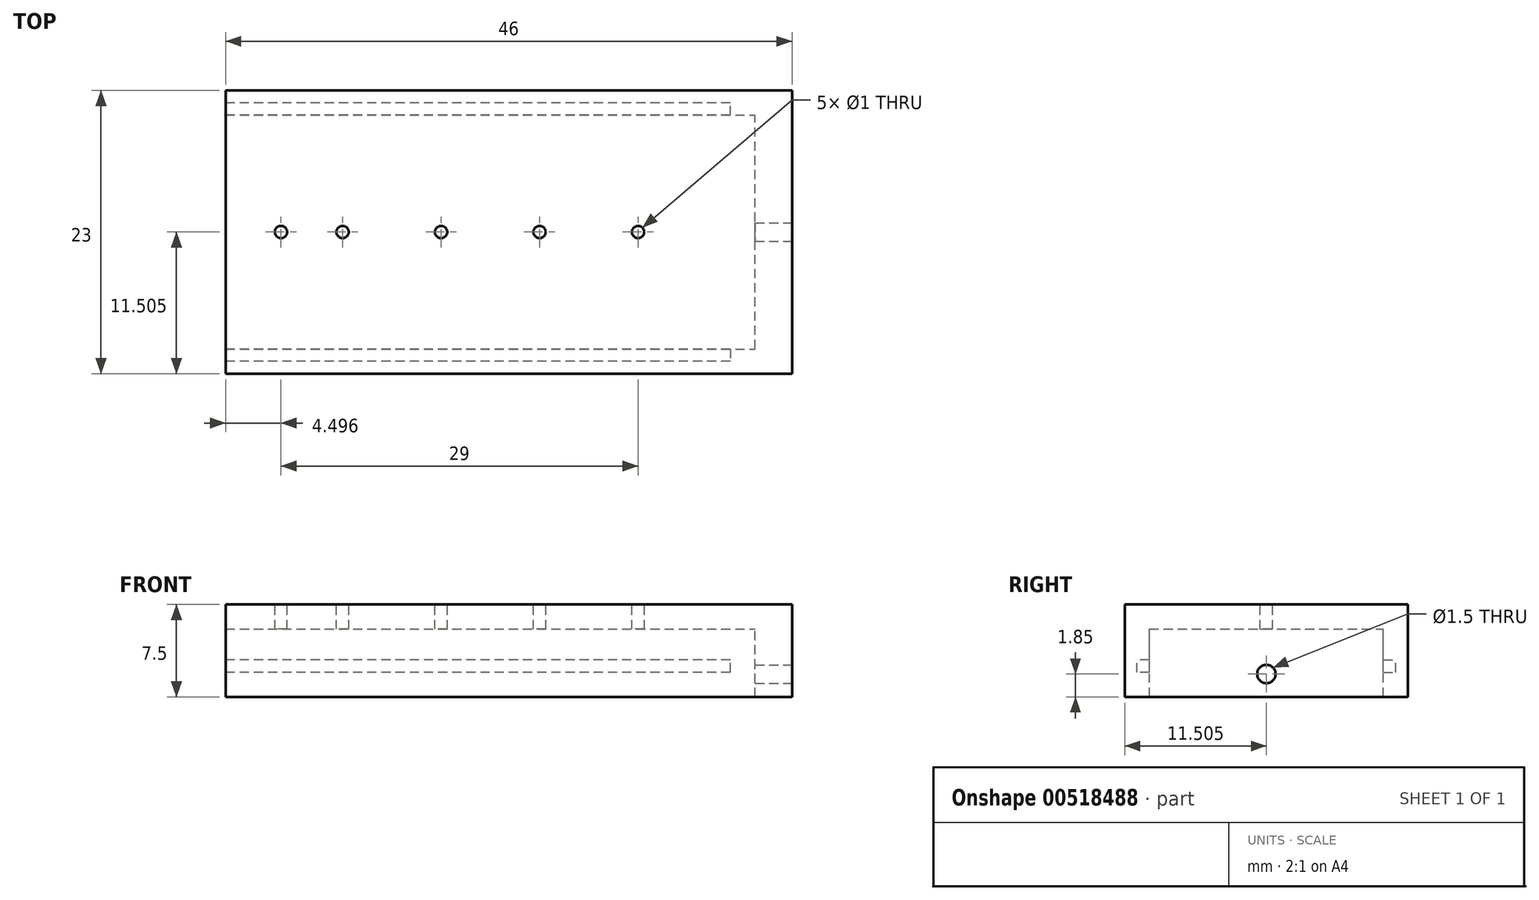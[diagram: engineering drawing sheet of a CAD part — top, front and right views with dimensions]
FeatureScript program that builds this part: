
annotation { "Feature Type Name" : "Feature", "Feature Type Description" : "" }
export const myFeature = defineFeature(function(context is Context, id is Id, definition is map)
    precondition{}
    {
        {
            var Q0;
            Q0=qCreatedBy(makeId("Top.planeOp"),FACE);
            var sketch = newSketch(context, id + "F0", { "sketchPlane" : qUnion([Q0])});
            skLineSegment(sketch, "E0.bottom", {"start": v(-4.4, -2.74) * mm, "end": v(41.6, -2.74) * mm});
            skLineSegment(sketch, "E0.top", {"start": v(-4.4, 20.26) * mm, "end": v(41.6, 20.26) * mm});
            skLineSegment(sketch, "E0.left", {"start": v(-4.4, -2.74) * mm, "end": v(-4.4, 20.26) * mm});
            skLineSegment(sketch, "E0.right", {"start": v(41.6, -2.74) * mm, "end": v(41.6, 20.26) * mm});
            skLineSegment(sketch, "E1.bottom", {"start": v(-4.4, -0.74) * mm, "end": v(38.6, -0.74) * mm});
            skLineSegment(sketch, "E1.top", {"start": v(-4.4, 18.26) * mm, "end": v(38.6, 18.26) * mm});
            skLineSegment(sketch, "E1.left", {"start": v(-4.4, -0.74) * mm, "end": v(-4.4, 18.26) * mm});
            skLineSegment(sketch, "E1.right", {"start": v(38.6, -0.74) * mm, "end": v(38.6, 18.26) * mm});
            skLineSegment(sketch, "E2", {"start": v(-5.45, 8.76) * mm, "end": v(42.38, 8.76) * mm, "construction": true});
            skPoint(sketch, "E2.startSnap0", {"position": v(-4.4, 8.76) * mm});
            skPoint(sketch, "E2.endSnap0", {"position": v(-4.4, 8.76) * mm});
            skPoint(sketch, "E3", {"position": v(38.6, 8.76) * mm});
            skPoint(sketch, "E4", {"position": v(41.6, 8.76) * mm});
            skSolve(sketch);
        }
        {
            var Q0;
            Q0=makeQuery(id+"F0.imprint","IMPRINT",FACE,{"disambiguationData":[TD([[makeQuery(id+"F0.imprint","IMPRINT",EDGE,{"derivedFrom":sQuery(id+"F0.wireOp",EDGE,"E1.bottom")}),1.0]])]});
            var Q1;
            {var subQ4=sQuery(id+"F0.wireOp",EDGE,"E0.bottom");Q1=makeQuery(id+"F0.imprint","IMPRINT",FACE,{"disambiguationData":[TD([[makeQuery(id+"F0.imprint","IMPRINT",EDGE,{"derivedFrom":subQ4}),1.0]])]});}
            extrude(context, id + "F1", {"entities" : qUnion([Q0, Q1]), "depth" : 2 * mm, "offsetDistance" : 25 * mm});
        }
        {
            var Q0;
            {var subQ4=sQuery(id+"F0.wireOp",EDGE,"E0.bottom");Q0=makeQuery(id+"F0.imprint","IMPRINT",FACE,{"disambiguationData":[TD([[makeQuery(id+"F0.imprint","IMPRINT",EDGE,{"derivedFrom":subQ4}),1.0]])]});}
            extrude(context, id + "F2", {"entities" : qUnion([Q0]), "operationType" : NewBodyOperationType.ADD, "oppositeDirection" : true, "depth" : 5.5 * mm, "offsetDistance" : 25 * mm});
        }
        {
            var Q0;
            {var subQ0=sQuery(id+"F0.wireOp",EDGE,"E0.left");var subQ1=sQuery(id+"F0.wireOp",EDGE,"E1.left");Q0=makeQuery(id+"F2.boolean.opBoolean","MERGE",FACE,{"derivedFrom":[makeQuery(id+"F1.opExtrude","SWEPT_FACE",FACE,{"disambiguationData":[OSD([subQ0,subQ1])]}),makeQuery(id+"F2.opExtrude","SWEPT_FACE",FACE,{"disambiguationData":[OSD([subQ0]),TDD([makeQuery(id+"F0.imprint","IMPRINT",EDGE,{"disambiguationData":[TD([[makeQuery(id+"F0.imprint","INTERSECT",VERTEX,{"derivedFrom":[sQuery(id+"F0.wireOp",EDGE,"E0.bottom"),subQ0]}),-1.0]])],"derivedFrom":subQ0})])]}),makeQuery(id+"F2.opExtrude","SWEPT_FACE",FACE,{"disambiguationData":[OSD([subQ0]),TDD([makeQuery(id+"F0.imprint","IMPRINT",EDGE,{"disambiguationData":[TD([[makeQuery(id+"F0.imprint","INTERSECT",VERTEX,{"derivedFrom":[sQuery(id+"F0.wireOp",EDGE,"E0.top"),subQ0]}),1.0]])],"derivedFrom":subQ0})])]})]});}
            var sketch = newSketch(context, id + "F3", { "sketchPlane" : qUnion([Q0])});
            skLineSegment(sketch, "E5", {"start": v(-8.76, 1.64) * mm, "end": v(-8.76, -7.83) * mm, "construction": true});
            skPoint(sketch, "E5.startSnap0", {"position": v(-8.76, 0) * mm});
            skPoint(sketch, "E6.oppositeSnap0", {"position": v(-18.26, -2.5) * mm});
            skLineSegment(sketch, "E6.bottom", {"start": v(-18.26, -3.5) * mm, "end": v(-19.26, -3.5) * mm});
            skLineSegment(sketch, "E6.top", {"start": v(-18.26, -2.5) * mm, "end": v(-19.26, -2.5) * mm});
            skLineSegment(sketch, "E6.left", {"start": v(-18.26, -3.5) * mm, "end": v(-18.26, -2.5) * mm});
            skLineSegment(sketch, "E6.right", {"start": v(-19.26, -3.5) * mm, "end": v(-19.26, -2.5) * mm});
            skLineSegment(sketch, "E7.MirrorCS", {"start": v(0.74, -2.5) * mm, "end": v(1.74, -2.5) * mm});
            skLineSegment(sketch, "E8.MirrorCS", {"start": v(1.74, -3.5) * mm, "end": v(1.74, -2.5) * mm});
            skLineSegment(sketch, "E9.MirrorCS", {"start": v(0.74, -3.5) * mm, "end": v(1.74, -3.5) * mm});
            skLineSegment(sketch, "E10.MirrorCS", {"start": v(0.74, -3.5) * mm, "end": v(0.74, -2.5) * mm});
            skSolve(sketch);
        }
        {
            var Q0;
            Q0=makeQuery(id+"F3.imprint","IMPRINT",FACE,{"disambiguationData":[TD([[makeQuery(id+"F3.imprint","IMPRINT",EDGE,{"derivedFrom":sQuery(id+"F3.wireOp",EDGE,"E6.bottom")}),-1.0]])]});
            var Q1;
            Q1=makeQuery(id+"F3.imprint","IMPRINT",FACE,{"disambiguationData":[TD([[makeQuery(id+"F3.imprint","IMPRINT",EDGE,{"derivedFrom":sQuery(id+"F3.wireOp",EDGE,"E7.MirrorCS")}),-1.0]])]});
            extrude(context, id + "F4", {"entities" : qUnion([Q0, Q1]), "operationType" : NewBodyOperationType.REMOVE, "oppositeDirection" : true, "depth" : 41 * mm, "offsetDistance" : 25 * mm});
        }
        {
            var Q0;
            {var subQ0=sQuery(id+"F0.wireOp",EDGE,"E0.right");Q0=makeQuery(id+"F2.boolean.opBoolean","MERGE",FACE,{"derivedFrom":[makeQuery(id+"F1.opExtrude","SWEPT_FACE",FACE,{"disambiguationData":[OSD([subQ0])]}),makeQuery(id+"F2.opExtrude","SWEPT_FACE",FACE,{"disambiguationData":[OSD([subQ0])]})]});}
            var sketch = newSketch(context, id + "F5", { "sketchPlane" : qUnion([Q0])});
            skCircle(sketch, "E11", {"center": v(8.76, -3.65) * mm, "radius": 0.75 * mm});
            skPoint(sketch, "E11.centerSnap0", {"position": v(8.76, 2) * mm});
            skSolve(sketch);
        }
        {
            var Q0;
            Q0=makeQuery(id+"F5.imprint","IMPRINT",FACE,{"disambiguationData":[TD([[makeQuery(id+"F5.imprint","IMPRINT",EDGE,{"derivedFrom":sQuery(id+"F5.wireOp",EDGE,"E11")}),1.0]])]});
            var Q1;
            Q1=makeQuery(id+"F1.opExtrude","SWEPT_BODY",BODY,{"disambiguationData":[OSD([sQuery(id+"F0.wireOp",EDGE,"E0.bottom"),sQuery(id+"F0.wireOp",EDGE,"E0.top"),sQuery(id+"F0.wireOp",EDGE,"E0.left"),sQuery(id+"F0.wireOp",EDGE,"E0.right"),sQuery(id+"F0.wireOp",EDGE,"E1.left")])]});
            extrude(context, id + "F6", {"entities" : qUnion([Q0]), "operationType" : NewBodyOperationType.REMOVE, "endBound" : BoundingType.UP_TO_BODY, "oppositeDirection" : true, "depth" : 25 * mm, "endBoundEntityBody" : qUnion([Q1]), "offsetDistance" : 25 * mm});
        }
        {
            var Q0;
            Q0=makeQuery(id+"F1.opExtrude","CAP_FACE",FACE,{"disambiguationData":[OSD([sQuery(id+"F0.wireOp",EDGE,"E0.bottom"),sQuery(id+"F0.wireOp",EDGE,"E0.top"),sQuery(id+"F0.wireOp",EDGE,"E0.left"),sQuery(id+"F0.wireOp",EDGE,"E0.right"),sQuery(id+"F0.wireOp",EDGE,"E1.left")])],"isStart":false});
            var sketch = newSketch(context, id + "F7", { "sketchPlane" : qUnion([Q0])});
            skCircle(sketch, "E12", {"center": v(5.1, 8.76) * mm, "radius": 0.5 * mm});
            skPoint(sketch, "E12.centerSnap0", {"position": v(-4.4, 8.76) * mm});
            skLineSegment(sketch, "E13", {"start": v(-4.4, 8.76) * mm, "end": v(41.6, 8.76) * mm, "construction": true});
            skCircle(sketch, "E14.1.0.0", {"center": v(13.1, 8.76) * mm, "radius": 0.5 * mm});
            skCircle(sketch, "E14.2.0.0", {"center": v(21.1, 8.76) * mm, "radius": 0.5 * mm});
            skCircle(sketch, "E14.3.0.0", {"center": v(29.1, 8.76) * mm, "radius": 0.5 * mm});
            skLineSegment(sketch, "E14.direction1", {"start": v(5.1, 8.76) * mm, "end": v(13.1, 8.76) * mm, "construction": true});
            skCircle(sketch, "E15", {"center": v(0.1, 8.76) * mm, "radius": 0.5 * mm});
            skSolve(sketch);
        }
        {
            var Q0;
            Q0=makeQuery(id+"F7.imprint","IMPRINT",FACE,{"disambiguationData":[TD([[makeQuery(id+"F7.imprint","IMPRINT",EDGE,{"derivedFrom":sQuery(id+"F7.wireOp",EDGE,"E12")}),1.0]])]});
            var Q1;
            Q1=makeQuery(id+"F7.imprint","IMPRINT",FACE,{"disambiguationData":[TD([[makeQuery(id+"F7.imprint","IMPRINT",EDGE,{"derivedFrom":sQuery(id+"F7.wireOp",EDGE,"E14.1.0.0")}),1.0]])]});
            var Q2;
            Q2=makeQuery(id+"F7.imprint","IMPRINT",FACE,{"disambiguationData":[TD([[makeQuery(id+"F7.imprint","IMPRINT",EDGE,{"derivedFrom":sQuery(id+"F7.wireOp",EDGE,"E14.2.0.0")}),1.0]])]});
            var Q3;
            Q3=makeQuery(id+"F7.imprint","IMPRINT",FACE,{"disambiguationData":[TD([[makeQuery(id+"F7.imprint","IMPRINT",EDGE,{"derivedFrom":sQuery(id+"F7.wireOp",EDGE,"E14.3.0.0")}),1.0]])]});
            var Q4;
            Q4=makeQuery(id+"F7.imprint","IMPRINT",FACE,{"disambiguationData":[TD([[makeQuery(id+"F7.imprint","IMPRINT",EDGE,{"derivedFrom":sQuery(id+"F7.wireOp",EDGE,"E15")}),1.0]])]});
            var Q5;
            Q5=makeQuery(id+"F1.opExtrude","SWEPT_BODY",BODY,{"disambiguationData":[OSD([sQuery(id+"F0.wireOp",EDGE,"E0.bottom"),sQuery(id+"F0.wireOp",EDGE,"E0.top"),sQuery(id+"F0.wireOp",EDGE,"E0.left"),sQuery(id+"F0.wireOp",EDGE,"E0.right"),sQuery(id+"F0.wireOp",EDGE,"E1.left")])]});
            extrude(context, id + "F8", {"entities" : qUnion([Q0, Q1, Q2, Q3, Q4]), "operationType" : NewBodyOperationType.REMOVE, "endBound" : BoundingType.UP_TO_BODY, "oppositeDirection" : true, "depth" : 25 * mm, "endBoundEntityBody" : qUnion([Q5]), "offsetDistance" : 25 * mm});
        }
    });
